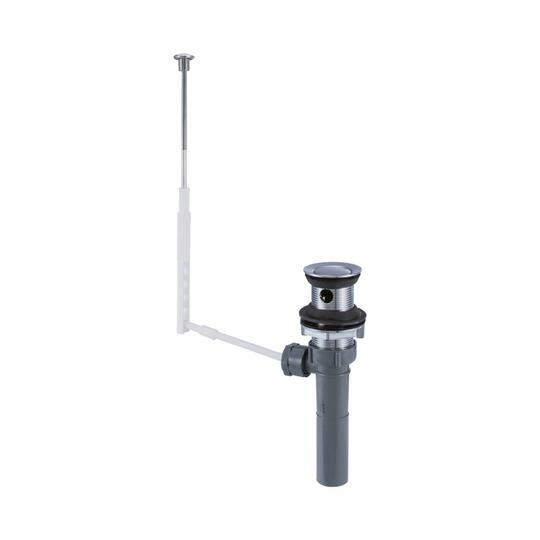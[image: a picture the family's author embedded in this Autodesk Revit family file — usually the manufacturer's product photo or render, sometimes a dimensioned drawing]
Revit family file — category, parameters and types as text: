
# Revit family: BIM_01-1933-04
name_source: partatom
category: Aparatos sanitarios
units: mm (PartAtom-declared; Revit-internal decimal feet)

## family parameters
Activar corte en vistas = No
Anfitrión = Cara
Compartido = No
Corte con vacíos al cargar = No
Cota de conector redondo = Usar diámetro
Mantener orientación de anotación = No
Número OmniClass = 23.31.11.00
Punto de cálculo de habitación = No
Tipo de pieza = Normal

## types (1)
- 01-1933-04
    Alto = 419 mm
    Alto desague = 210 mm  [stored 0.688976 ft]
    Ancho = 53 mm  [stored 0.173885 ft]
    Caucho = Caucho
    Conexiones = Tubo para acople en tubería de 1¼"
    Conexión AC = Sí
    Conexión AF = Sí
    Conexión de residuos = No
    Conexión de ventilación = No
    Consumo aproximado a 25 psi = 27
    Date Modified = 25-08-2025
    Descripción = Desague Automatico
    Diametro Externo = 1 1/4"
    Elevación por defecto = 0 mm  [stored 0 ft]
    Fabricante = Gricol
    Garantia Especifica = 20 Años
    Goteo de Sello = 63 ml/min
    Imagen de tipo = FOTO DESAGÜE AUTOMÁTICO CON REBOSE GRIS - CROMO.jpg
    Link Ficha Tecnica = https://infotecnica.gricol.com
    Materiales del producto = ABS, Caucho, Latón, Polipropileno, Acetal (POM).
    Modelo = 01-1933-04
    Plastico ABS = Plastico - ABS Cromado
    Plastico Gris = Plastico - polipropileno + colorante gris
    Product Name = Desagüe Automático Con Rebose
    Profundidad = 177 mm  [stored 0.580709 ft]
    Referente Normativo = NTC 5302, ASME A112.18.2 / CSA B125.2
    Resistencia a Corrosión = NTC 1156, Sal Neutral
    Sitio web = https://www.gricol.com
    Temperaturas de trabajo = de 19C° A 62C°
    Tipo de Uso = Domestico
    Torque de Conexioón = 20 Nm
    URL = https://www.gricol.com
    Vida Util = 100000 Ciclos

note: [stored X ft] marks values corroborated as IEEE doubles in the binary element streams (Revit-internal decimal feet)

## geometry (parser evidence)
native form markers: Blend x2, Sweep x3
no freeform markers — native parametric forms only
